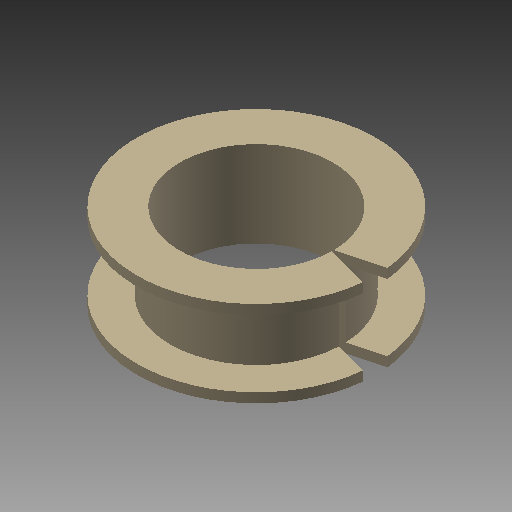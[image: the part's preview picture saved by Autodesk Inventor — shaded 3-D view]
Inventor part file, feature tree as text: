
AUTODESK INVENTOR PART (.ipt)
format: ipt  version: 2019 (Build 230136000, 136)  size: 148,480 bytes
history: native  units: mm
features: sketch x2, revolve x1, extrude x1
ambient origin geometry x8: Origin, YZ Plane, XZ Plane, XY Plane, X Axis, Y Axis, Z Axis, Center Point
bodies: Solid1 (feature_tree)
feature tree (4):
  revolve  "Revolution1"  [1 undecoded]
  extrude  "Extrusion1"  Depth=0.5mm
  sketch  "Sketch1"  dims[d0=8.0mm d1=9.0mm]
  sketch  "Sketch2"  dims[d2=12.5mm d3=0.5mm d4=3.5mm d5=0.5mm d6=90.0deg d8=15.0deg d9=30.0deg d10=2.21673mm d11=2.21673mm d12=10.0mm d13=0.0mm]
note: 1 required parameter value undecoded (feature->parameter linkage not recoverable at this tier; creation-order binding heuristic only, values carry confidence <= 0.55)
